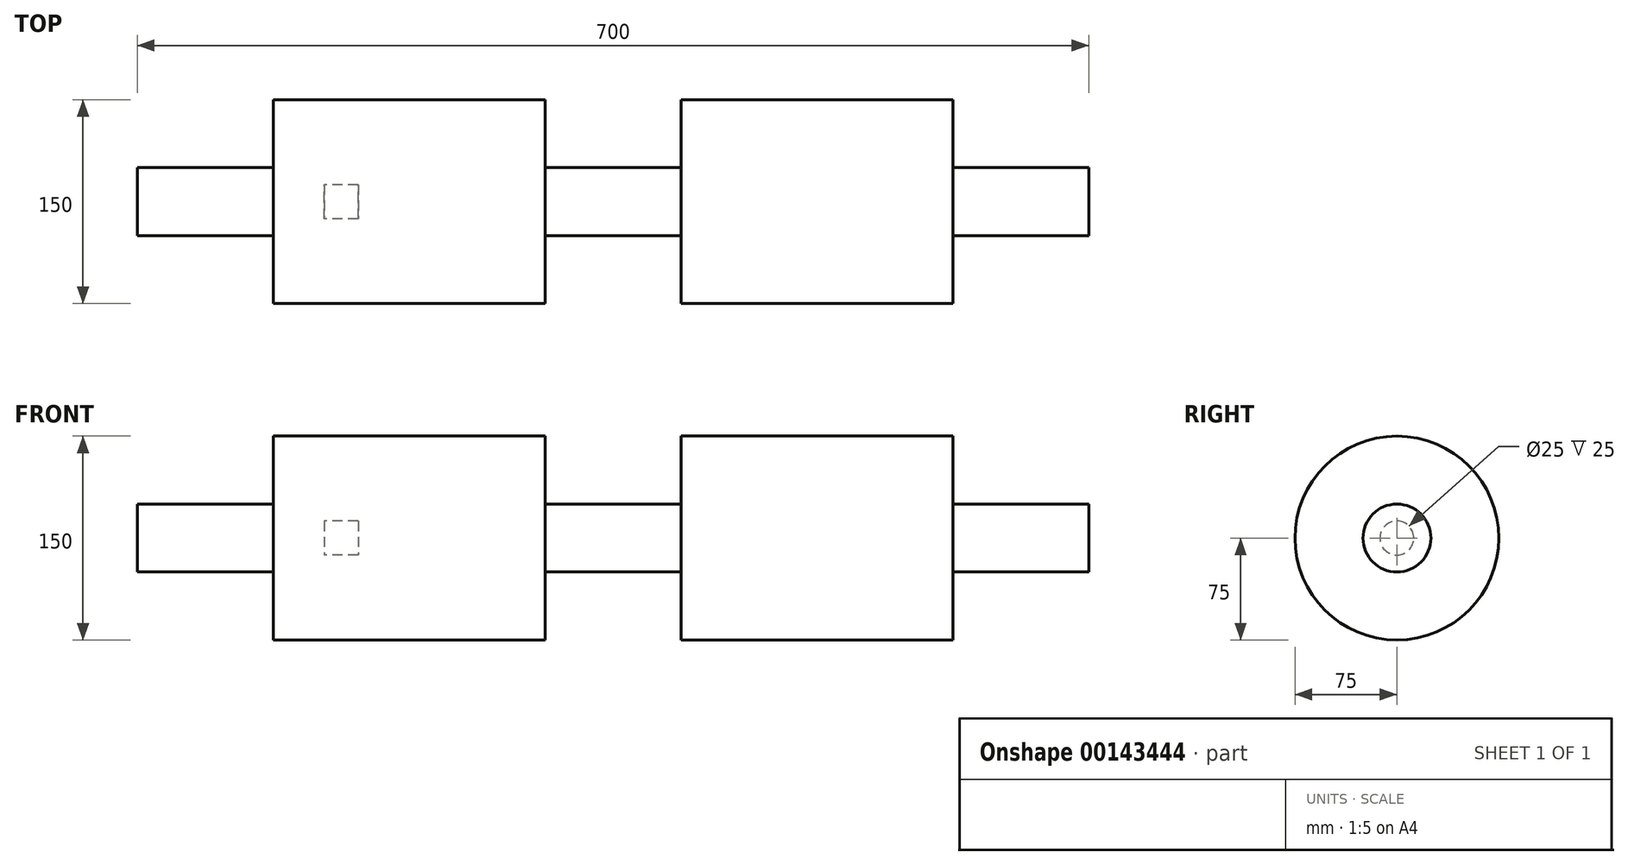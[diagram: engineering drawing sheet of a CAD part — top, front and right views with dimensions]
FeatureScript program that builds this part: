
annotation { "Feature Type Name" : "Feature", "Feature Type Description" : "" }
export const myFeature = defineFeature(function(context is Context, id is Id, definition is map)
    precondition{}
    {
        {
            var Q0;
            Q0=qCreatedBy(makeId("Top.planeOp"),FACE);
            var sketch = newSketch(context, id + "F0", { "sketchPlane" : qUnion([Q0])});
            skLineSegment(sketch, "E0.top", {"start": v(-100, 75) * mm, "end": v(100, 75) * mm});
            skPoint(sketch, "E0.middle", {"position": v(0, 0) * mm});
            skLineSegment(sketch, "E1.bottom", {"start": v(-100, 25) * mm, "end": v(-200, 25) * mm});
            skLineSegment(sketch, "E2", {"start": v(-100, 25) * mm, "end": v(-100, 75) * mm});
            skLineSegment(sketch, "E3", {"start": v(-200, 25) * mm, "end": v(-200, 75) * mm});
            skLineSegment(sketch, "E4", {"start": v(-200, 75) * mm, "end": v(-400, 75) * mm});
            skLineSegment(sketch, "E5", {"start": v(-400, 75) * mm, "end": v(-400, 25) * mm});
            skLineSegment(sketch, "E6", {"start": v(-400, 25) * mm, "end": v(-500, 25) * mm});
            skLineSegment(sketch, "E7", {"start": v(100, 75) * mm, "end": v(100, 25) * mm});
            skLineSegment(sketch, "E8", {"start": v(100, 25) * mm, "end": v(200, 25) * mm});
            skLineSegment(sketch, "E9.bottom", {"start": v(-362.5, 12.5) * mm, "end": v(-337.5, 12.5) * mm});
            skPoint(sketch, "E9.middle", {"position": v(-350, 0) * mm});
            skLineSegment(sketch, "E10", {"start": v(-500, 25) * mm, "end": v(-500, 0) * mm});
            skLineSegment(sketch, "E11", {"start": v(200, 0) * mm, "end": v(200, 25) * mm});
            skLineSegment(sketch, "E12", {"start": v(-337.5, 12.5) * mm, "end": v(-337.5, 0) * mm});
            skLineSegment(sketch, "E13", {"start": v(-362.5, 0) * mm, "end": v(-362.5, 12.5) * mm});
            skLineSegment(sketch, "E14", {"start": v(-500, 0) * mm, "end": v(-362.5, 0) * mm});
            skLineSegment(sketch, "E15", {"start": v(-337.5, 0) * mm, "end": v(200, 0) * mm});
            skSolve(sketch);
        }
        {
            var Q0;
            Q0 = qSketchRegion(id + "F0", true);
            var Q1;
            Q1=sQuery(id+"F0.wireOp",EDGE,"E15");
            revolve(context, id + "F1", {"entities" : qUnion([Q0]), "axis" : qUnion([Q1]), "revolveType" : RevolveType.FULL});
        }
    });
